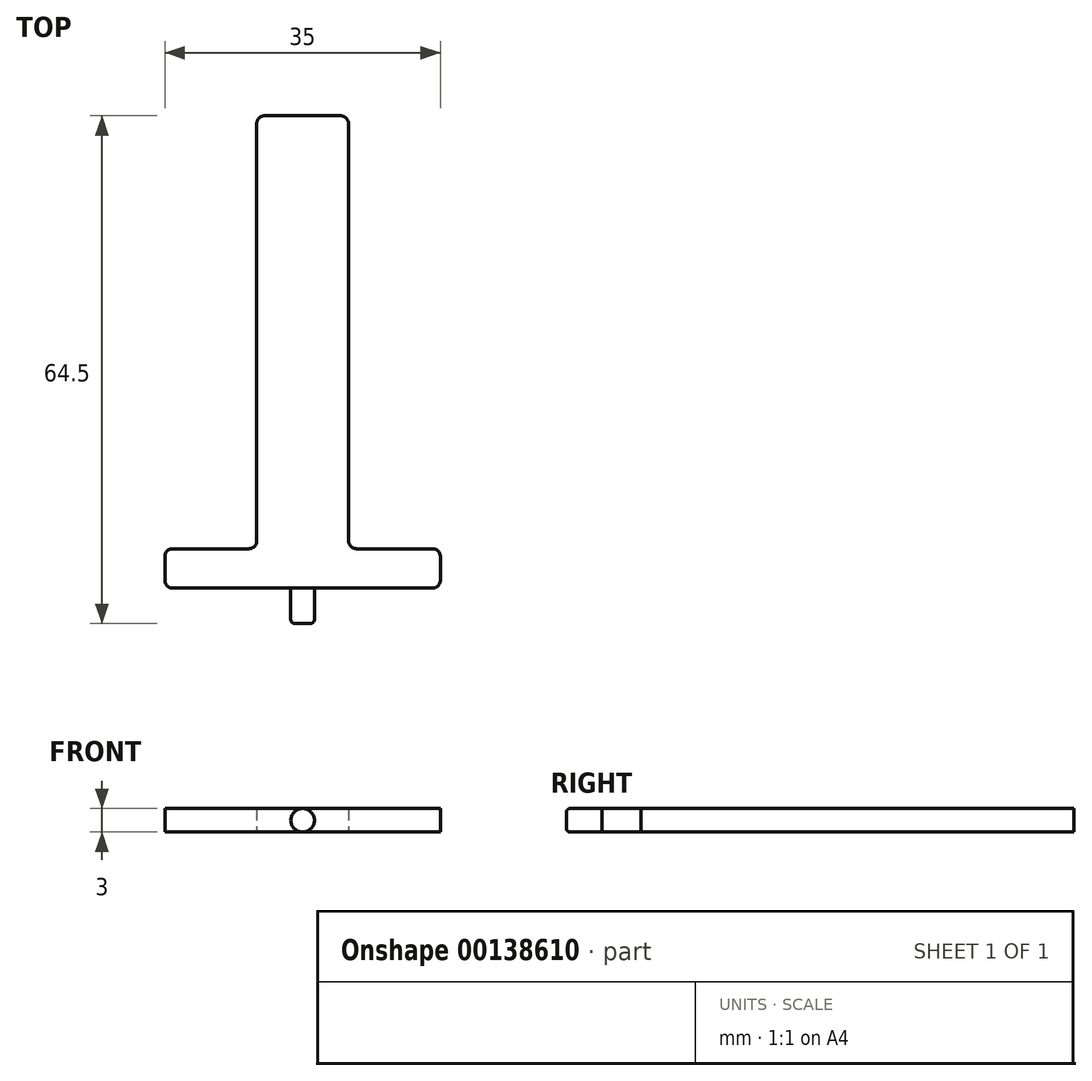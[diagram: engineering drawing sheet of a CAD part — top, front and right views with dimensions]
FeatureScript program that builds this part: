
annotation { "Feature Type Name" : "Feature", "Feature Type Description" : "" }
export const myFeature = defineFeature(function(context is Context, id is Id, definition is map)
    precondition{}
    {
        {
            assignVariable(context, id + "F0", {"name" : "pin_dia", "anyValue" : 3 * mm});
        }
        {
            assignVariable(context, id + "F1", {"name" : "pin_length", "anyValue" : 4.5 * mm});
        }
        {
            assignVariable(context, id + "F2", {"name" : "pin_end_fillet", "anyValue" : 0.5 * mm});
        }
        {
            var Q0;
            Q0=qCreatedBy(makeId("Top.planeOp"),FACE);
            var sketch = newSketch(context, id + "F3", { "sketchPlane" : qUnion([Q0])});
            skLineSegment(sketch, "E0", {"start": v(1, 0) * mm, "end": v(34, 0) * mm});
            skLineSegment(sketch, "E1", {"start": v(35, 1) * mm, "end": v(35, 4) * mm});
            skLineSegment(sketch, "E2", {"start": v(34, 5) * mm, "end": v(24.33, 5) * mm});
            skLineSegment(sketch, "E3", {"start": v(23.33, 6) * mm, "end": v(23.33, 59) * mm});
            skLineSegment(sketch, "E4", {"start": v(22.33, 60) * mm, "end": v(12.67, 60) * mm});
            skLineSegment(sketch, "E5", {"start": v(11.67, 59) * mm, "end": v(11.67, 6) * mm});
            skLineSegment(sketch, "E6", {"start": v(10.67, 5) * mm, "end": v(1, 5) * mm});
            skLineSegment(sketch, "E7", {"start": v(0, 4) * mm, "end": v(0, 1) * mm});
            skPoint(sketch, "E8.visualSharp", {"position": v(11.67, 60) * mm});
            skArc(sketch, "E8.filletArc", {"start": v(12.67, 60) * mm, "mid": v(11.96, 59.7) * mm, "end": v(11.67, 59) * mm});
            skPoint(sketch, "E9.visualSharp", {"position": v(23.33, 60) * mm});
            skArc(sketch, "E9.filletArc", {"start": v(23.33, 59) * mm, "mid": v(23.04, 59.7) * mm, "end": v(22.33, 60) * mm});
            skPoint(sketch, "E10.visualSharp", {"position": v(23.33, 5) * mm});
            skArc(sketch, "E10.filletArc", {"start": v(23.33, 6) * mm, "mid": v(23.63, 5.3) * mm, "end": v(24.33, 5) * mm});
            skPoint(sketch, "E11.visualSharp", {"position": v(35, 5) * mm});
            skArc(sketch, "E11.filletArc", {"start": v(35, 4) * mm, "mid": v(34.7, 4.7) * mm, "end": v(34, 5) * mm});
            skPoint(sketch, "E12.visualSharp", {"position": v(35, 0) * mm});
            skArc(sketch, "E12.filletArc", {"start": v(34, 0) * mm, "mid": v(34.7, 0.3) * mm, "end": v(35, 1) * mm});
            skPoint(sketch, "E13.visualSharp", {"position": v(11.67, 5) * mm});
            skArc(sketch, "E13.filletArc", {"start": v(10.67, 5) * mm, "mid": v(11.37, 5.3) * mm, "end": v(11.67, 6) * mm});
            skPoint(sketch, "E14.visualSharp", {"position": v(0, 0) * mm});
            skArc(sketch, "E14.filletArc", {"start": v(0, 1) * mm, "mid": v(0.3, 0.3) * mm, "end": v(1, 0) * mm});
            skPoint(sketch, "E15.visualSharp", {"position": v(0, 5) * mm});
            skArc(sketch, "E15.filletArc", {"start": v(1, 5) * mm, "mid": v(0.3, 4.7) * mm, "end": v(0, 4) * mm});
            skSolve(sketch);
        }
        {
            var Q0;
            Q0=makeQuery(id+"F3.imprint","IMPRINT",FACE,{"disambiguationData":[TD([[makeQuery(id+"F3.imprint","IMPRINT",EDGE,{"derivedFrom":sQuery(id+"F3.wireOp",EDGE,"E0")}),1.0]])]});
            extrude(context, id + "F4", {"entities" : qUnion([Q0]), "depth" : getVariable(context, 'pin_dia')});
        }
        {
            var Q0;
            Q0=makeQuery(id+"F4.opExtrude","SWEPT_FACE",FACE,{"disambiguationData":[OSD([sQuery(id+"F3.wireOp",EDGE,"E0")])]});
            var sketch = newSketch(context, id + "F5", { "sketchPlane" : qUnion([Q0])});
            skLineSegment(sketch, "E16.0", {"start": v(1, 3) * mm, "end": v(34, 3) * mm, "construction": true});
            skLineSegment(sketch, "E17.0", {"start": v(1, 0) * mm, "end": v(34, 0) * mm, "construction": true});
            skLineSegment(sketch, "E18", {"start": v(17.5, 3) * mm, "end": v(17.5, 0) * mm, "construction": true});
            skCircle(sketch, "E19", {"center": v(17.5, 1.5) * mm, "radius": 1.5 * mm});
            skSolve(sketch);
        }
        {
            var Q0;
            {var subQ0=sQuery(id+"F5.wireOp",EDGE,"E19");var subQ1=sQuery(id+"F3.wireOp",EDGE,"E0");var subQ2=makeQuery(id+"F5.imprint","INTERSECT",VERTEX,{"derivedFrom":[makeQuery(id+"F4.opExtrude","CAP_EDGE",EDGE,{"disambiguationData":[OSD([subQ1])],"isStart":true}),subQ0]});Q0=makeQuery(id+"F5.imprint","IMPRINT",FACE,{"disambiguationData":[TD([[makeQuery(id+"F5.imprint","IMPRINT",EDGE,{"disambiguationData":[TD([[subQ2,1.0]])],"derivedFrom":subQ0}),1.0]])]});}
            extrude(context, id + "F6", {"entities" : qUnion([Q0]), "operationType" : NewBodyOperationType.ADD, "depth" : getVariable(context, 'pin_length')});
        }
        {
            var Q0;
            Q0=makeQuery(id+"F6.opExtrude","CAP_EDGE",EDGE,{"disambiguationData":[OSD([sQuery(id+"F5.wireOp",EDGE,"E19")])],"isStart":false});
            fillet(context, id + "F7", {"entities" : qUnion([Q0]), "radius" : getVariable(context, 'pin_end_fillet'), "tangentPropagation" : true, "allowEdgeOverflow" : false});
        }
    });
